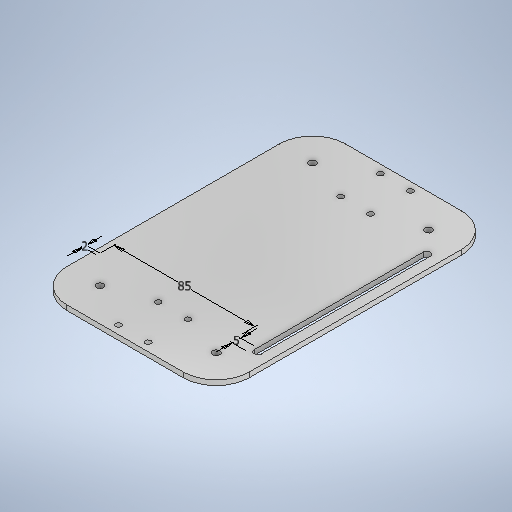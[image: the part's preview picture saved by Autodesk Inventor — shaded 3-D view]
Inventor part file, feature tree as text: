
AUTODESK INVENTOR PART (.ipt)
format: ipt  version: 2025.2 (Build 292293000, 293)  size: 308,736 bytes
history: native  units: mm
features: sketch x4, plane x3, extrude x2, hole x2, fillet x1
ambient origin geometry x8: Origin, YZ Plane, XZ Plane, XY Plane, X Axis, Y Axis, Z Axis, Center Point
bodies: Solid1 (feature_tree)
feature tree (12):
  sketch  "Sketch1"  dims[d4=110.0mm d5=168.0mm]
  extrude  "Extrusion2"  Depth=168.0mm
  hole  "Hole1"  [1 undecoded]
  fillet  "Fillet1"  Radius=18.0mm
  plane  "Work Plane1"
  plane  "Work Plane2"
  hole  "Hole2"  [1 undecoded]
  extrude  "Extrusion3"  Depth=4.3mm
  plane  "Work Plane3"
  sketch  "Sketch5"  dims[d26=18.0mm d27=24.0mm d28=3.4mm d29=6.0mm d30=4.0mm d31=2.0mm d32=90.0deg d33=8.0mm d34=20.594885mm d35=20.0mm d36=-84.0mm d37=-55.0mm d38=4.3mm d39=6.0mm d40=4.0mm d41=2.0mm d42=90.0deg d43=8.0mm d44=20.594885mm d45=8.0mm d46=102.0mm d47=8.0mm d48=4.3mm d49=0.0mm d50=0.0mm d51=5.0mm d52=2.0mm d53=85.0mm]
  sketch  "Sketch2"  dims[d20=3.0mm d21=0.0mm d22=5.0mm d23=18.0mm]
  sketch  "Sketch4"  dims[d24=24.0mm d25=5.0mm]
note: 2 required parameter values undecoded (feature->parameter linkage not recoverable at this tier; creation-order binding heuristic only, values carry confidence <= 0.55)
